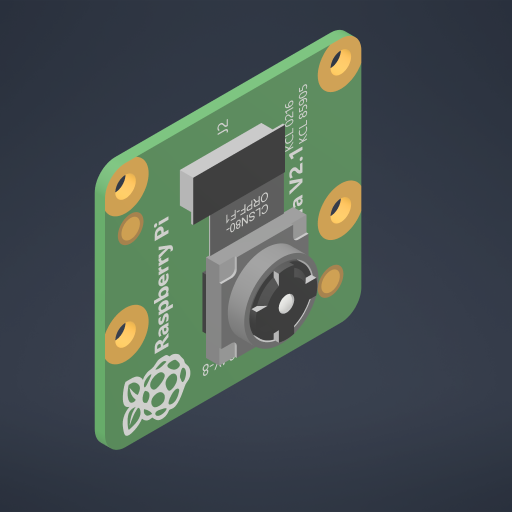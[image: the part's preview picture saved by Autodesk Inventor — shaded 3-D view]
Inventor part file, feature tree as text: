
AUTODESK INVENTOR PART (.ipt)
format: ipt  version: 2023 (Build 270158000, 158)  size: 2,926,592 bytes
history: native  units: mm
features: sketch x3, other x2, plane x2, projected_geometry x1
ambient origin geometry x8: Origin, YZ Plane, XZ Plane, XY Plane, X Axis, Y Axis, Z Axis, Center Point
bodies: Solid1 (feature_tree), Body1 (feature_tree)
feature tree (8):
  other  "Decal1"
  plane  "Work Plane1"
  sketch  "Sketch2"  dims[d52=200.0mm]
  plane  "Work Plane2"
  sketch  "Sketch3"  dims[d54=4.258603mm d55=5.427974mm]
  sketch  "Sketch1"  dims[d45=0.0mm]
  other  "Image1"
  projected_geometry  "Projected Loop1"
